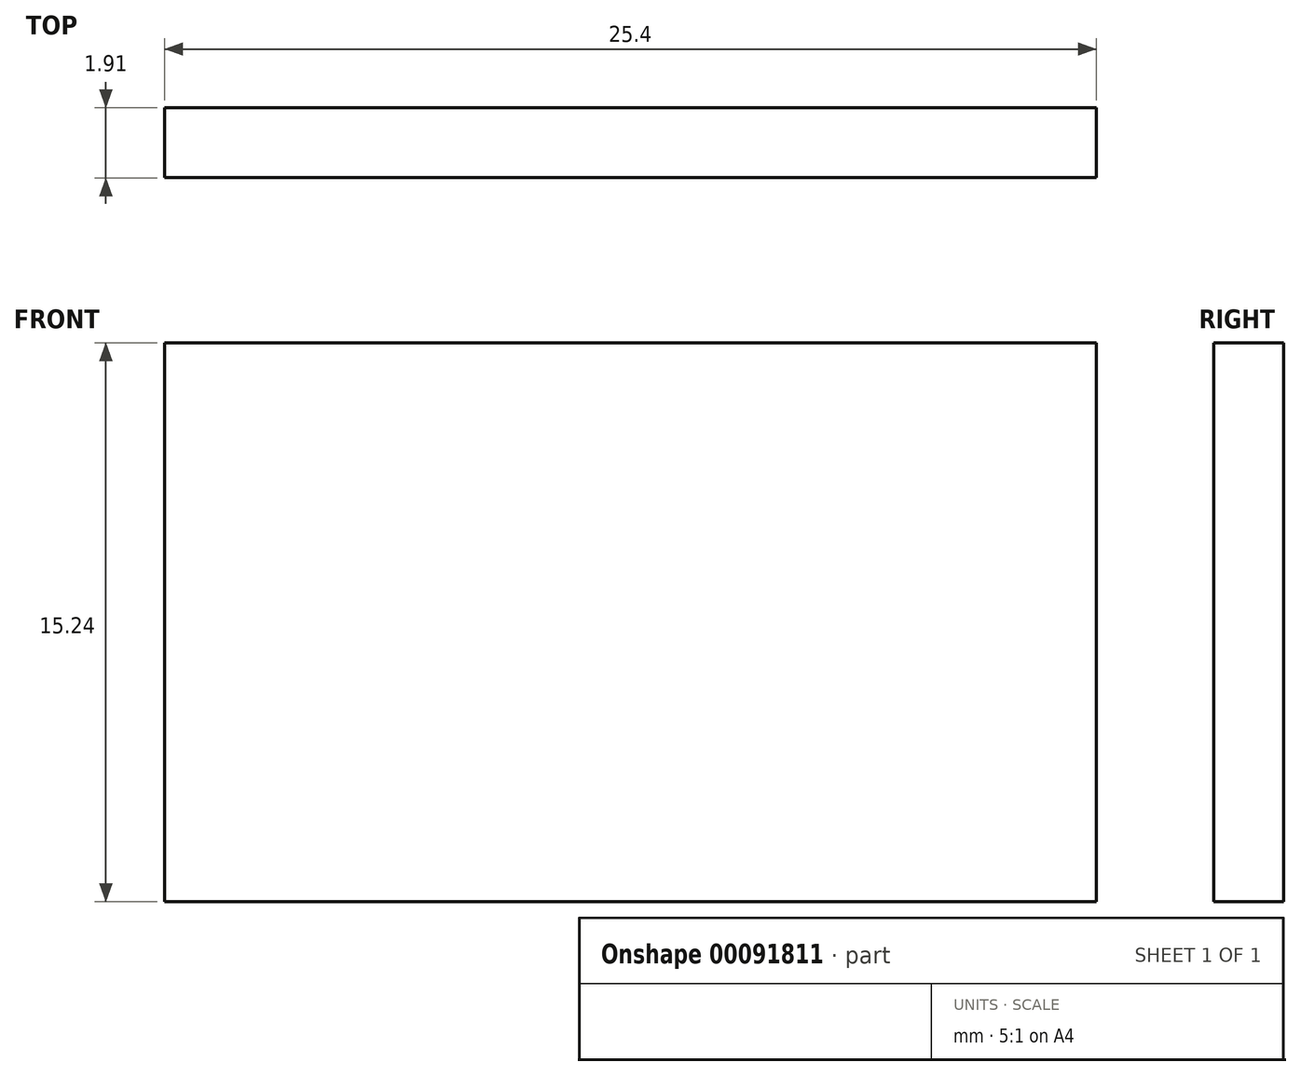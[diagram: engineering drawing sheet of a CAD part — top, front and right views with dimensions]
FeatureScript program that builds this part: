
annotation { "Feature Type Name" : "Feature", "Feature Type Description" : "" }
export const myFeature = defineFeature(function(context is Context, id is Id, definition is map)
    precondition{}
    {
        {
            var Q0;
            Q0=qCreatedBy(makeId("Front.planeOp"),FACE);
            var sketch = newSketch(context, id + "F0", { "sketchPlane" : qUnion([Q0])});
            skLineSegment(sketch, "E0.bottom", {"start": v(14.63, -7.62) * mm, "end": v(-10.77, -7.62) * mm});
            skLineSegment(sketch, "E0.top", {"start": v(14.63, 7.62) * mm, "end": v(-10.77, 7.62) * mm});
            skLineSegment(sketch, "E0.left", {"start": v(14.63, -7.62) * mm, "end": v(14.63, 7.62) * mm});
            skLineSegment(sketch, "E0.right", {"start": v(-10.77, -7.62) * mm, "end": v(-10.77, 7.62) * mm});
            skPoint(sketch, "E0.middle", {"position": v(1.93, 0) * mm});
            skSolve(sketch);
        }
        {
            var Q0;
            Q0=makeQuery(id+"F0.imprint","IMPRINT",FACE,{"disambiguationData":[TD([[makeQuery(id+"F0.imprint","IMPRINT",EDGE,{"derivedFrom":sQuery(id+"F0.wireOp",EDGE,"E0.bottom")}),-1.0]])]});
            extrude(context, id + "F1", {"entities" : qUnion([Q0]), "depth" : 1.9 * mm});
        }
    });
